# Revit family: Accessory-Flush_Actuator_Plate-KOHLER-BEAM-K-23056T
name_source: partatom
category: Specialty Equipment
revit_build: Autodesk Revit 2017 (Build: 20160225_1515(x64)
units: mm (PartAtom-declared; Revit-internal decimal feet)

## family parameters
Cut with Voids When Loaded = No
Host = Face
OmniClass Number = 23.31.25.00
OmniClass Title = Toilet and Bath Specialties
Part Type = Normal
Room Calculation Point = No
Round Connector Dimension = Use Diameter
Shared = No

## types (8) — shared parameters
ADA Compliant = No
Assembly Code = C1030200
Date Modified = 01/13/2021
Default Elevation = 42"
Description = BEAM Bo Ming induction water tank panel
Height = 6 5/16"
Length = 7/16"
Manufacturer = KOHLER Co.
Master Format 2014 = 10 28 00
Master Format 2014 Name = Toilet, Bath, and Laundry Accessories
Material = Premium Metal Construction
Product Name = BEAM
URL = http://www.kohler.com.cn
WaterSense Certified = No
Width = 8 7/8"

## per-type parameters (varying)
| type | Finish | Model | Product Documentation Link | Product Page URL | Type |
| BS- Brushed Stainless | Kohler-Metal-BS-Brushed_Stainless | K-23056T-BS |  |  | 5 |
| CP- Polished Chrome | Kohler-Metal-CP-Polished_Chrome | K-23056T-CP | https://files.kohler.com.cn | https://www.kohler.com.cn | 1 |
| AF- Flange Gold | Kohler-Metal-AF-Flange_Gold | K-23056T-AF |  |  | 2 |
| 2BL- Original Black | Kohler-Metal-2BL-Original_Black | K-23056T-2BL |  |  | 3 |
| BN- Roman Silver | Kohler-Metal-BN-Roman_Silver | K-23056T-BN |  |  | 4 |
| BV- Roman Copper | Kohler-Metal-BV-Roman_Copper | K-23056T-BV |  |  | 6 |
| TT- Titanium Silver | Kohler-Metal-TT-Titanium_Silver | K-23056T-TT |  |  | 7 |
| RGD- Rose Gold | Kohler-Metal-RGD-Rose_Gold | K-23056T-RGD |  |  | 8 |

## geometry (parser evidence)
native form markers: Sweep x6
no freeform markers — native parametric forms only
